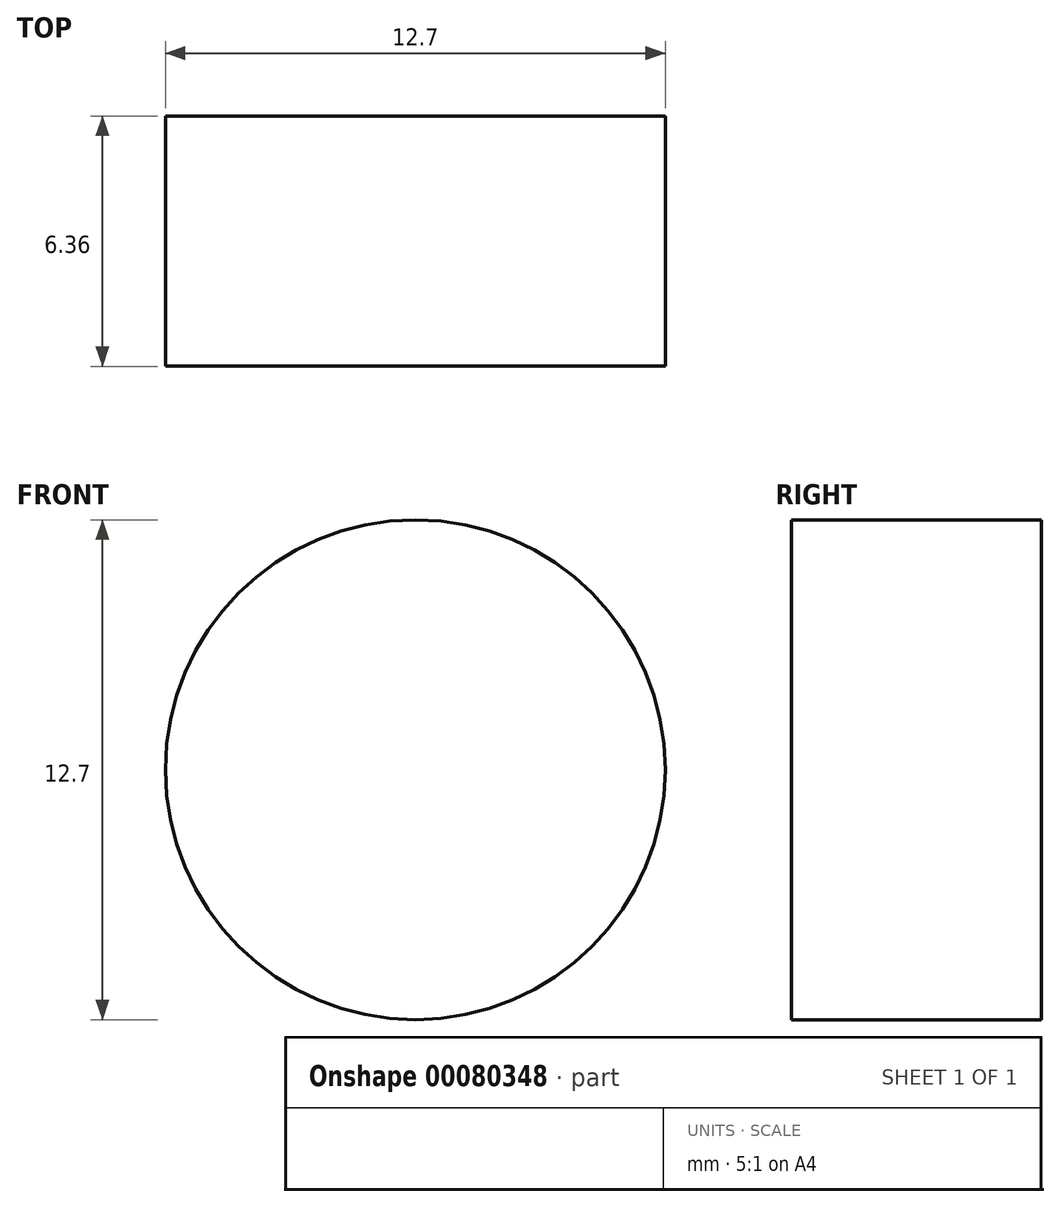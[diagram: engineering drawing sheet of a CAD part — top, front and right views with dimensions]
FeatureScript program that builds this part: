
annotation { "Feature Type Name" : "Feature", "Feature Type Description" : "" }
export const myFeature = defineFeature(function(context is Context, id is Id, definition is map)
    precondition{}
    {
        {
            var Q0;
            Q0=qCreatedBy(makeId("Front.planeOp"),FACE);
            var sketch = newSketch(context, id + "F0", { "sketchPlane" : qUnion([Q0])});
            skCircle(sketch, "E0", {"center": v(0, 0) * mm, "radius": 6.35 * mm});
            skSolve(sketch);
        }
        {
            var Q0;
            Q0=makeQuery(id+"F0.imprint","IMPRINT",FACE,{"disambiguationData":[TD([[makeQuery(id+"F0.imprint","IMPRINT",EDGE,{"derivedFrom":sQuery(id+"F0.wireOp",EDGE,"E0")}),1.0]])]});
            extrude(context, id + "F1", {"entities" : qUnion([Q0]), "endBound" : BoundingType.SYMMETRIC, "depth" : 6.35 * mm});
        }
    });
